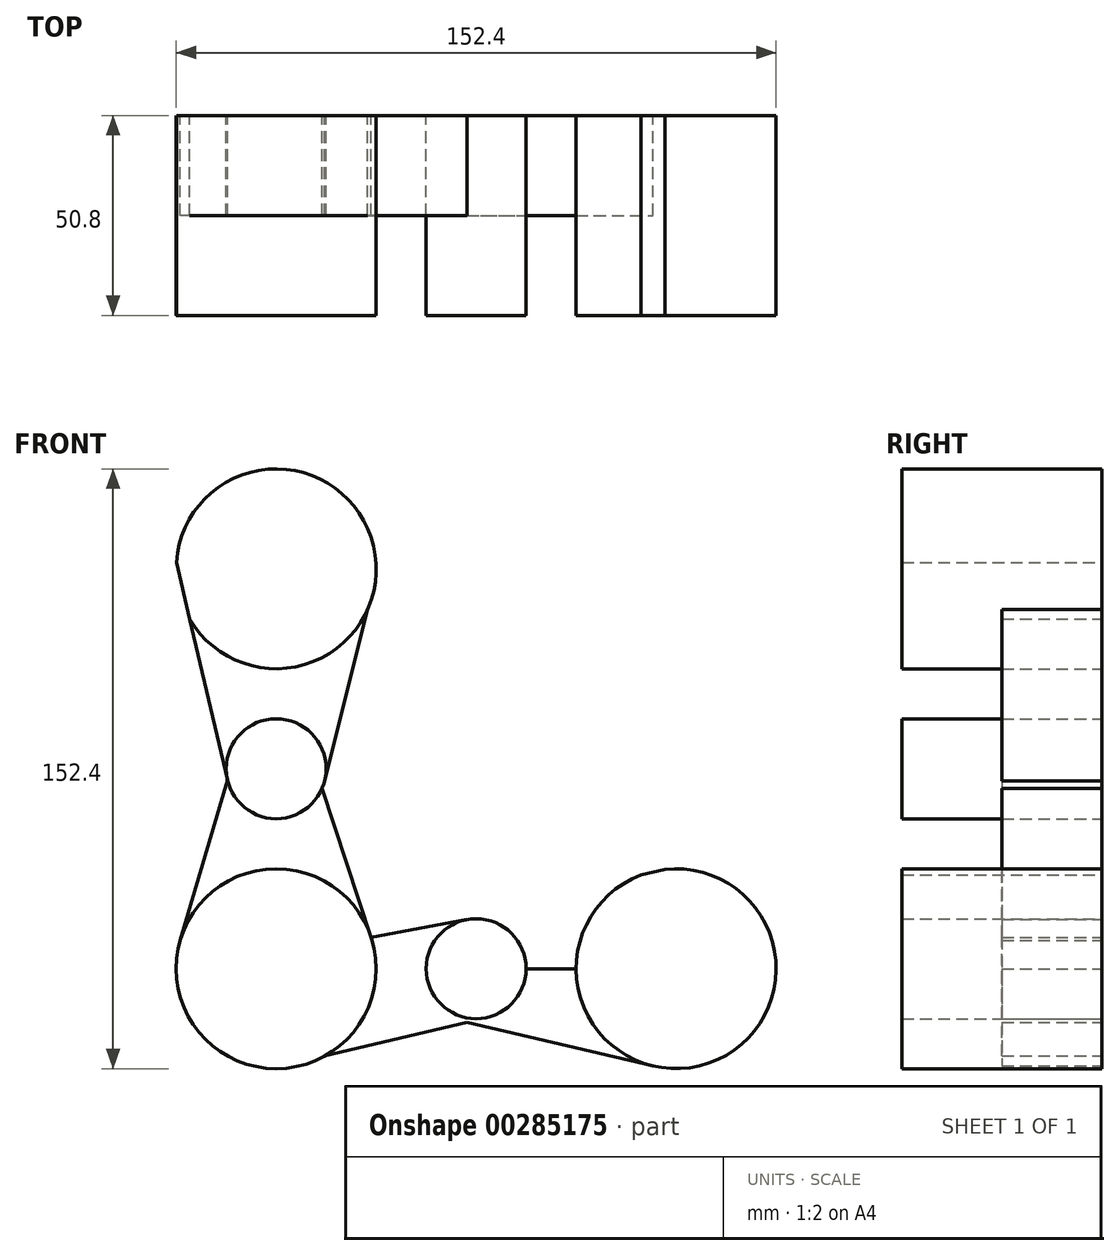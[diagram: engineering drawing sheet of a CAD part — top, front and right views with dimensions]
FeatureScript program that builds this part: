
annotation { "Feature Type Name" : "Feature", "Feature Type Description" : "" }
export const myFeature = defineFeature(function(context is Context, id is Id, definition is map)
    precondition{}
    {
        {
            var Q0;
            Q0=qCreatedBy(makeId("Front.planeOp"),FACE);
            var sketch = newSketch(context, id + "F0", { "sketchPlane" : qUnion([Q0])});
            skLineSegment(sketch, "E0", {"start": v(-101.6, -63.49) * mm, "end": v(-50.8, -63.49) * mm});
            skLineSegment(sketch, "E1", {"start": v(-50.8, -63.49) * mm, "end": v(0, -63.49) * mm});
            skLineSegment(sketch, "E2", {"start": v(-101.6, -63.49) * mm, "end": v(-101.6, -12.69) * mm});
            skLineSegment(sketch, "E3", {"start": v(-101.6, -12.69) * mm, "end": v(-101.6, 38.11) * mm});
            skCircle(sketch, "E4", {"center": v(-101.6, 38.11) * mm, "radius": 25.4 * mm});
            skCircle(sketch, "E5", {"center": v(-101.6, -63.49) * mm, "radius": 25.4 * mm});
            skCircle(sketch, "E6", {"center": v(0, -63.49) * mm, "radius": 25.4 * mm});
            skCircle(sketch, "E7", {"center": v(-101.6, -12.69) * mm, "radius": 12.7 * mm});
            skCircle(sketch, "E8", {"center": v(-50.8, -63.49) * mm, "radius": 12.7 * mm});
            skLineSegment(sketch, "E9", {"start": v(-126.95, 39.73) * mm, "end": v(-113.96, -15.59) * mm});
            skLineSegment(sketch, "E10", {"start": v(-78.37, 27.83) * mm, "end": v(-89.28, -15.77) * mm});
            skLineSegment(sketch, "E11", {"start": v(-113.96, -15.59) * mm, "end": v(-125.96, -56.3) * mm});
            skLineSegment(sketch, "E12", {"start": v(-89.93, -17.7) * mm, "end": v(-77.47, -55.54) * mm});
            skLineSegment(sketch, "E13", {"start": v(-77.47, -55.54) * mm, "end": v(-53.13, -51) * mm});
            skLineSegment(sketch, "E14", {"start": v(-89.28, -85.7) * mm, "end": v(-53.13, -77.1) * mm});
            skLineSegment(sketch, "E15", {"start": v(-53.48, -50.47) * mm, "end": v(-2.88, -38.25) * mm});
            skLineSegment(sketch, "E16", {"start": v(-53.13, -77.1) * mm, "end": v(-5.8, -88.21) * mm});
            skSolve(sketch);
        }
        {
            var Q0;
            {var subQ0=sQuery(id+"F0.wireOp",EDGE,"E4");var subQ1=makeQuery(id+"F0.imprint","INTERSECT",VERTEX,{"derivedFrom":[sQuery(id+"F0.wireOp",EDGE,"E3"),subQ0]});Q0=makeQuery(id+"F0.imprint","IMPRINT",FACE,{"disambiguationData":[TD([[makeQuery(id+"F0.imprint","IMPRINT",EDGE,{"disambiguationData":[TD([[subQ1,1.0]])],"derivedFrom":subQ0}),1.0]])]});}
            var Q1;
            {var subQ0=sQuery(id+"F0.wireOp",EDGE,"E9");var subQ1=sQuery(id+"F0.wireOp",EDGE,"E4");var subQ2=makeQuery(id+"F0.imprint","INTERSECT",VERTEX,{"disambiguationData":[OD(0.0)],"derivedFrom":[subQ1,subQ0]});Q1=makeQuery(id+"F0.imprint","IMPRINT",FACE,{"disambiguationData":[TD([[makeQuery(id+"F0.imprint","IMPRINT",EDGE,{"disambiguationData":[TD([[subQ2,-1.0]])],"derivedFrom":subQ1}),1.0]])]});}
            var Q2;
            {var subQ0=sQuery(id+"F0.wireOp",EDGE,"E3");var subQ1=sQuery(id+"F0.wireOp",EDGE,"E2");var subQ2=makeQuery(id+"F0.imprint","INTERSECT",VERTEX,{"derivedFrom":[subQ1,subQ0]});Q2=makeQuery(id+"F0.imprint","IMPRINT",FACE,{"disambiguationData":[TD([[makeQuery(id+"F0.imprint","IMPRINT",EDGE,{"disambiguationData":[TD([[subQ2,1.0]])],"derivedFrom":subQ1}),1.0]])]});}
            var Q3;
            {var subQ3=sQuery(id+"F0.wireOp",EDGE,"E2");var subQ5=sQuery(id+"F0.wireOp",EDGE,"E3");var subQ6=makeQuery(id+"F0.imprint","INTERSECT",VERTEX,{"derivedFrom":[subQ3,subQ5]});Q3=makeQuery(id+"F0.imprint","IMPRINT",FACE,{"disambiguationData":[TD([[makeQuery(id+"F0.imprint","IMPRINT",EDGE,{"disambiguationData":[TD([[subQ6,1.0]])],"derivedFrom":subQ3}),-1.0]])]});}
            var Q4;
            {var subQ0=sQuery(id+"F0.wireOp",EDGE,"E2");var subQ1=sQuery(id+"F0.wireOp",EDGE,"E0");var subQ2=makeQuery(id+"F0.imprint","INTERSECT",VERTEX,{"derivedFrom":[subQ1,subQ0]});Q4=makeQuery(id+"F0.imprint","IMPRINT",FACE,{"disambiguationData":[TD([[makeQuery(id+"F0.imprint","IMPRINT",EDGE,{"disambiguationData":[TD([[subQ2,-1.0]])],"derivedFrom":subQ1}),1.0]])]});}
            var Q5;
            {var subQ3=sQuery(id+"F0.wireOp",EDGE,"E2");var subQ5=sQuery(id+"F0.wireOp",EDGE,"E0");var subQ6=makeQuery(id+"F0.imprint","INTERSECT",VERTEX,{"derivedFrom":[subQ5,subQ3]});Q5=makeQuery(id+"F0.imprint","IMPRINT",FACE,{"disambiguationData":[TD([[makeQuery(id+"F0.imprint","IMPRINT",EDGE,{"disambiguationData":[TD([[subQ6,-1.0]])],"derivedFrom":subQ5}),-1.0]])]});}
            var Q6;
            {var subQ0=sQuery(id+"F0.wireOp",EDGE,"E1");var subQ1=sQuery(id+"F0.wireOp",EDGE,"E0");var subQ2=makeQuery(id+"F0.imprint","INTERSECT",VERTEX,{"derivedFrom":[subQ1,subQ0]});Q6=makeQuery(id+"F0.imprint","IMPRINT",FACE,{"disambiguationData":[TD([[makeQuery(id+"F0.imprint","IMPRINT",EDGE,{"disambiguationData":[TD([[subQ2,1.0]])],"derivedFrom":subQ1}),-1.0]])]});}
            var Q7;
            {var subQ0=sQuery(id+"F0.wireOp",EDGE,"E1");var subQ1=sQuery(id+"F0.wireOp",EDGE,"E0");var subQ2=makeQuery(id+"F0.imprint","INTERSECT",VERTEX,{"derivedFrom":[subQ1,subQ0]});Q7=makeQuery(id+"F0.imprint","IMPRINT",FACE,{"disambiguationData":[TD([[makeQuery(id+"F0.imprint","IMPRINT",EDGE,{"disambiguationData":[TD([[subQ2,1.0]])],"derivedFrom":subQ1}),1.0]])]});}
            var Q8;
            {var subQ0=sQuery(id+"F0.wireOp",EDGE,"E6");var subQ1=makeQuery(id+"F0.imprint","INTERSECT",VERTEX,{"derivedFrom":[sQuery(id+"F0.wireOp",EDGE,"E1"),subQ0]});Q8=makeQuery(id+"F0.imprint","IMPRINT",FACE,{"disambiguationData":[TD([[makeQuery(id+"F0.imprint","IMPRINT",EDGE,{"disambiguationData":[TD([[subQ1,1.0]])],"derivedFrom":subQ0}),1.0]])]});}
            extrude(context, id + "F1", {"entities" : qUnion([Q0, Q1, Q2, Q3, Q4, Q5, Q6, Q7, Q8]), "depth" : 50.8 * mm});
        }
        {
            var Q0;
            {var subQ0=sQuery(id+"F0.wireOp",EDGE,"E4");var subQ1=sQuery(id+"F0.wireOp",EDGE,"E3");var subQ2=makeQuery(id+"F0.imprint","INTERSECT",VERTEX,{"derivedFrom":[subQ1,subQ0]});Q0=makeQuery(id+"F0.imprint","IMPRINT",FACE,{"disambiguationData":[TD([[makeQuery(id+"F0.imprint","IMPRINT",EDGE,{"disambiguationData":[TD([[subQ2,1.0]])],"derivedFrom":subQ1}),1.0]])]});}
            var Q1;
            {var subQ5=sQuery(id+"F0.wireOp",EDGE,"E10");Q1=makeQuery(id+"F0.imprint","IMPRINT",FACE,{"disambiguationData":[TD([[makeQuery(id+"F0.imprint","IMPRINT",EDGE,{"derivedFrom":subQ5}),-1.0]])]});}
            var Q2;
            {var subQ5=sQuery(id+"F0.wireOp",EDGE,"E12");Q2=makeQuery(id+"F0.imprint","IMPRINT",FACE,{"disambiguationData":[TD([[makeQuery(id+"F0.imprint","IMPRINT",EDGE,{"derivedFrom":subQ5}),-1.0]])]});}
            var Q3;
            {var subQ5=sQuery(id+"F0.wireOp",EDGE,"E11");Q3=makeQuery(id+"F0.imprint","IMPRINT",FACE,{"disambiguationData":[TD([[makeQuery(id+"F0.imprint","IMPRINT",EDGE,{"derivedFrom":subQ5}),1.0]])]});}
            var Q4;
            {var subQ5=sQuery(id+"F0.wireOp",EDGE,"E13");Q4=makeQuery(id+"F0.imprint","IMPRINT",FACE,{"disambiguationData":[TD([[makeQuery(id+"F0.imprint","IMPRINT",EDGE,{"derivedFrom":subQ5}),-1.0]])]});}
            var Q5;
            {var subQ0=sQuery(id+"F0.wireOp",EDGE,"E14");Q5=makeQuery(id+"F0.imprint","IMPRINT",FACE,{"disambiguationData":[TD([[makeQuery(id+"F0.imprint","IMPRINT",EDGE,{"derivedFrom":subQ0}),1.0]])]});}
            extrude(context, id + "F2", {"entities" : qUnion([Q0, Q1, Q2, Q3, Q4, Q5]), "depth" : 25.4 * mm});
        }
    });
